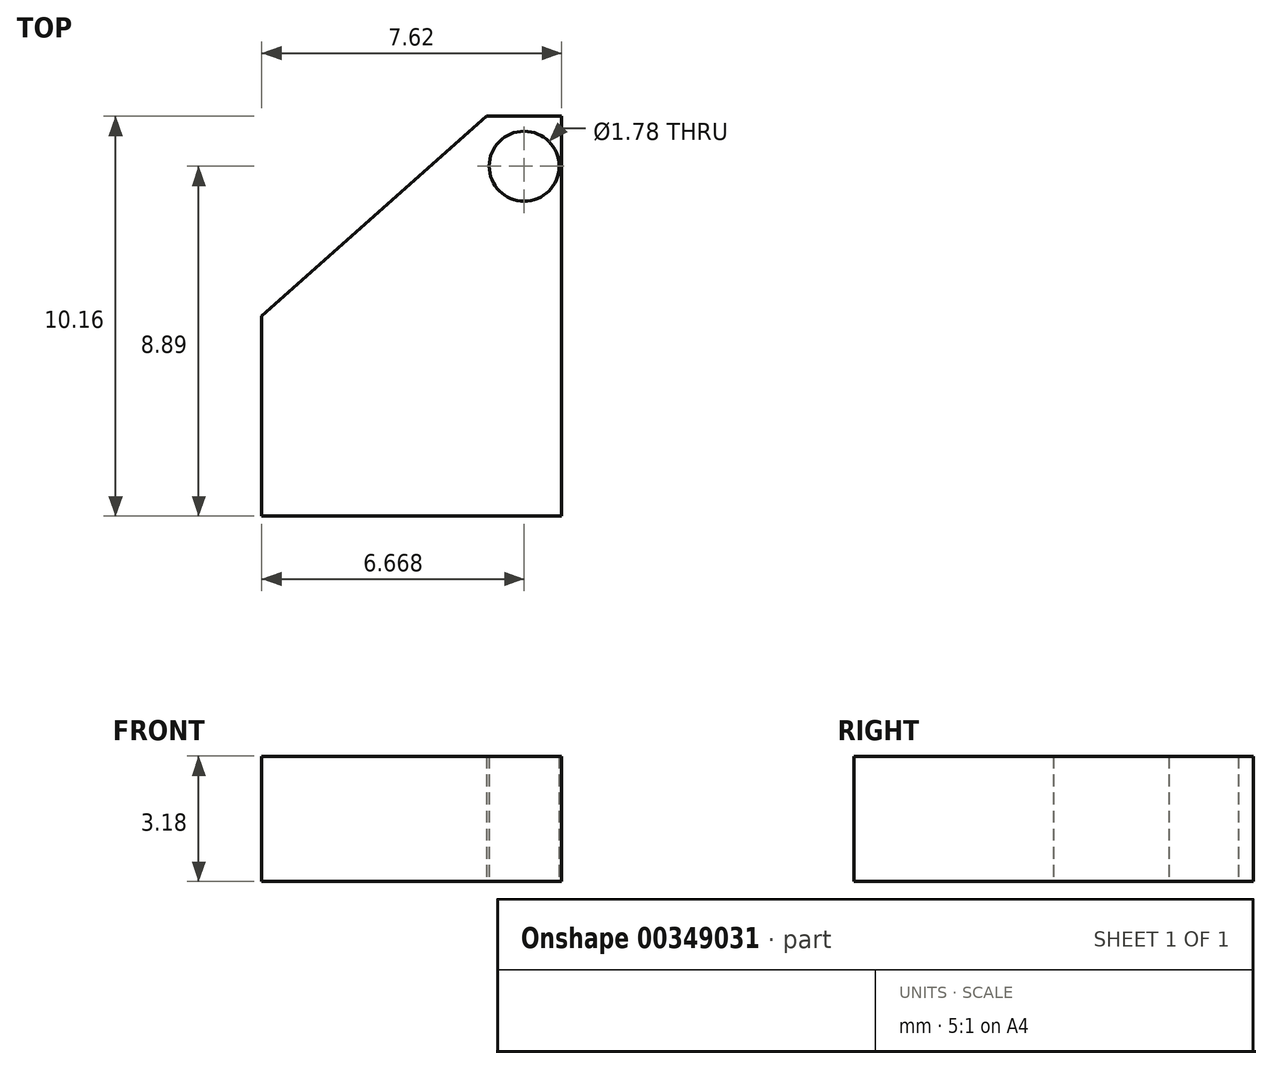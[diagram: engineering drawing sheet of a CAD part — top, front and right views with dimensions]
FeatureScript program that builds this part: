
annotation { "Feature Type Name" : "Feature", "Feature Type Description" : "" }
export const myFeature = defineFeature(function(context is Context, id is Id, definition is map)
    precondition{}
    {
        {
            var Q0;
            Q0=qCreatedBy(makeId("Top.planeOp"),FACE);
            var sketch = newSketch(context, id + "F0", { "sketchPlane" : qUnion([Q0])});
            skLineSegment(sketch, "E0.bottom", {"start": v(3.81, -5.08) * mm, "end": v(-3.81, -5.08) * mm});
            skLineSegment(sketch, "E0.top", {"start": v(3.81, 5.08) * mm, "end": v(1.9, 5.08) * mm});
            skLineSegment(sketch, "E0.left", {"start": v(3.81, -5.08) * mm, "end": v(3.81, 5.08) * mm});
            skLineSegment(sketch, "E0.right", {"start": v(-3.81, -5.08) * mm, "end": v(-3.81, 0) * mm});
            skPoint(sketch, "E0.middle", {"position": v(0, 0) * mm});
            skPoint(sketch, "E1", {"position": v(0, 5.08) * mm});
            skLineSegment(sketch, "E2", {"start": v(1.9, 5.08) * mm, "end": v(3.81, 5.08) * mm});
            skPoint(sketch, "E3", {"position": v(1.9, 5.08) * mm});
            skPoint(sketch, "E4", {"position": v(-3.81, 0) * mm});
            skLineSegment(sketch, "E5", {"start": v(1.9, 5.08) * mm, "end": v(-3.81, 0) * mm});
            skPoint(sketch, "E6.orphan", {"position": v(-3.81, 5.08) * mm});
            skLineSegment(sketch, "E7", {"start": v(3.81, 5.08) * mm, "end": v(3.81, 0) * mm});
            skLineSegment(sketch, "E8", {"start": v(3.81, 0) * mm, "end": v(3.81, 2.54) * mm});
            skLineSegment(sketch, "E9", {"start": v(3.81, 2.54) * mm, "end": v(1.9, 5.08) * mm});
            skPoint(sketch, "E10", {"position": v(2.86, 3.81) * mm});
            skSolve(sketch);
        }
        {
            var Q0;
            Q0 = qSketchRegion(id + "F0", true);
            extrude(context, id + "F1", {"entities" : qUnion([Q0]), "depth" : 3.17 * mm});
        }
        {
            var Q0;
            Q0=sQuery(id+"F0.wireOp",VERTEX,"E10");
            var Q1;
            Q1=makeQuery(id+"F1.opExtrude","SWEPT_BODY",BODY,{"disambiguationData":[OSD([sQuery(id+"F0.wireOp",EDGE,"E0.bottom"),sQuery(id+"F0.wireOp",EDGE,"E0.left"),sQuery(id+"F0.wireOp",EDGE,"E0.right"),sQuery(id+"F0.wireOp",EDGE,"E2"),sQuery(id+"F0.wireOp",EDGE,"E5"),sQuery(id+"F0.wireOp",EDGE,"E7"),sQuery(id+"F0.wireOp",EDGE,"E8")])]});
            hole(context, id + "F2", {"style" : HoleStyle.SIMPLE, "endStyle" : HoleEndStyle.THROUGH, "oppositeDirection" : true, "holeDiameter" : 1.78 * mm, "isTappedThrough" : true, "tappedDepth" : 12.7 * mm, "tapClearance" : 3, "locations" : qUnion([Q0]), "scope" : qUnion([Q1])});
        }
    });
